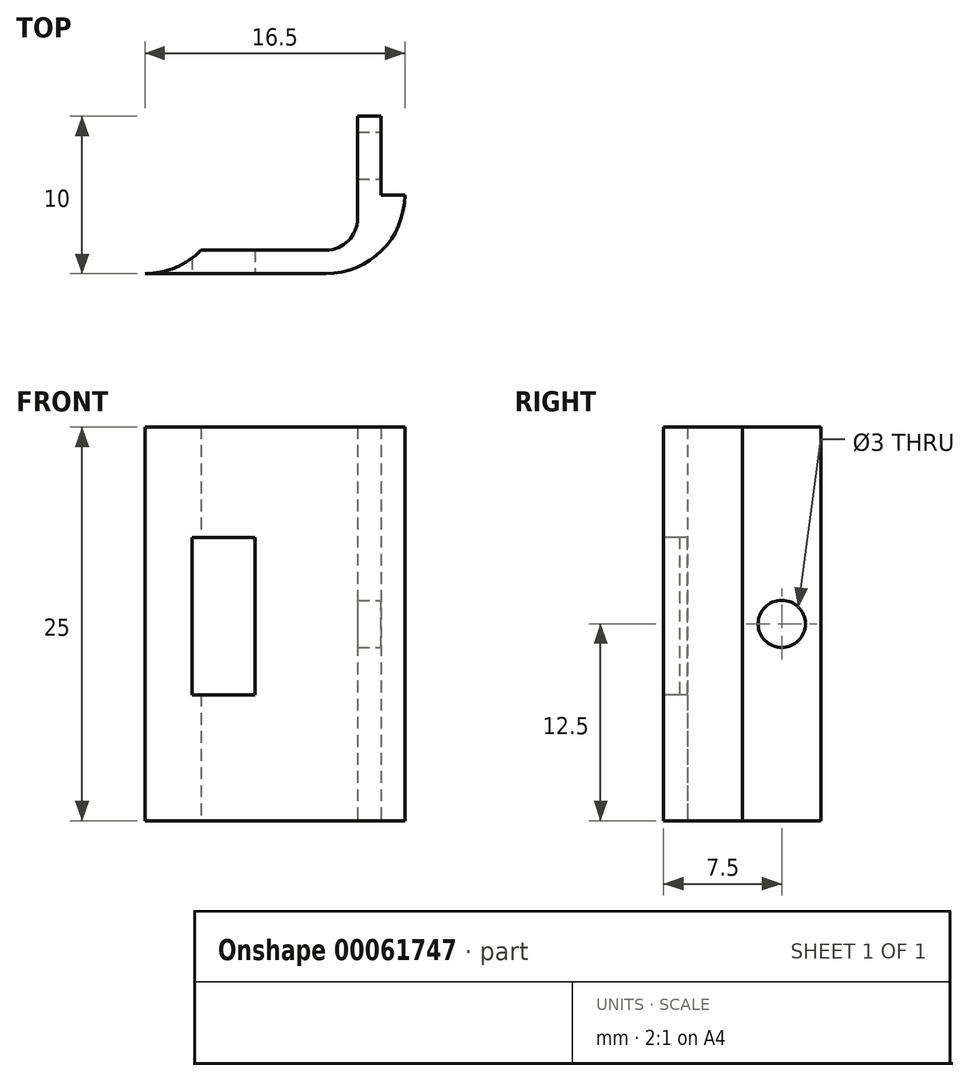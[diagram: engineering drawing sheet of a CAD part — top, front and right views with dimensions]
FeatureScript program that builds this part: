
annotation { "Feature Type Name" : "Feature", "Feature Type Description" : "" }
export const myFeature = defineFeature(function(context is Context, id is Id, definition is map)
    precondition{}
    {
        {
            var Q0;
            Q0=qCreatedBy(makeId("Top.planeOp"),FACE);
            var sketch = newSketch(context, id + "F0", { "sketchPlane" : qUnion([Q0])});
            skLineSegment(sketch, "E0", {"start": v(0, 0) * mm, "end": v(11.5, 0) * mm});
            skArc(sketch, "E1.filletArc", {"start": v(11.5, 0) * mm, "mid": v(15.04, 1.46) * mm, "end": v(16.5, 5) * mm});
            skLineSegment(sketch, "E2.1", {"start": v(0, 1.5) * mm, "end": v(10, 1.5) * mm});
            skLineSegment(sketch, "E3", {"start": v(0, 1.5) * mm, "end": v(0, 0) * mm});
            skCircle(sketch, "E4", {"center": v(0, 5) * mm, "radius": 5 * mm, "construction": true});
            skLineSegment(sketch, "E5", {"start": v(0, 1.5) * mm, "end": v(0, 8.16) * mm, "construction": true});
            skPoint(sketch, "E6", {"position": v(3.57, 1.5) * mm});
            skArc(sketch, "E7", {"start": v(0, 0) * mm, "mid": v(1.94, 0.4) * mm, "end": v(3.57, 1.5) * mm});
            skLineSegment(sketch, "E8", {"start": v(16.5, 5) * mm, "end": v(15, 5) * mm});
            skLineSegment(sketch, "E9", {"start": v(15, 5) * mm, "end": v(13.5, 5) * mm});
            skLineSegment(sketch, "E10", {"start": v(13.5, 5) * mm, "end": v(13.5, 10) * mm});
            skLineSegment(sketch, "E11", {"start": v(13.5, 10) * mm, "end": v(15, 10) * mm});
            skLineSegment(sketch, "E12", {"start": v(15, 10) * mm, "end": v(15, 5) * mm});
            skLineSegment(sketch, "E13", {"start": v(10, 1.5) * mm, "end": v(11.5, 1.5) * mm});
            skLineSegment(sketch, "E14", {"start": v(13.5, 3.5) * mm, "end": v(13.5, 5) * mm});
            skPoint(sketch, "E15.visualSharp", {"position": v(13.5, 1.5) * mm});
            skArc(sketch, "E15.filletArc", {"start": v(11.5, 1.5) * mm, "mid": v(12.91, 2.09) * mm, "end": v(13.5, 3.5) * mm});
            skSolve(sketch);
        }
        {
            var Q0;
            Q0=makeQuery(id+"F0.imprint","IMPRINT",FACE,{"disambiguationData":[TD([[makeQuery(id+"F0.imprint","IMPRINT",EDGE,{"derivedFrom":sQuery(id+"F0.wireOp",EDGE,"E0")}),1.0]])]});
            var Q1;
            Q1=makeQuery(id+"F0.imprint","IMPRINT",FACE,{"disambiguationData":[TD([[makeQuery(id+"F0.imprint","IMPRINT",EDGE,{"derivedFrom":sQuery(id+"F0.wireOp",EDGE,"E9")}),-1.0]])]});
            extrude(context, id + "F1", {"entities" : qUnion([Q0, Q1]), "depth" : 25 * mm});
        }
        {
            var Q0;
            Q0=makeQuery(id+"F1.opExtrude","SWEPT_FACE",FACE,{"disambiguationData":[OSD([sQuery(id+"F0.wireOp",EDGE,"E12")])]});
            var sketch = newSketch(context, id + "F2", { "sketchPlane" : qUnion([Q0])});
            skCircle(sketch, "E16", {"center": v(7.5, 12.5) * mm, "radius": 1.5 * mm});
            skPoint(sketch, "E17", {"position": v(7.5, 25) * mm});
            skPoint(sketch, "E18", {"position": v(-40.9, 34.48) * mm});
            skLineSegment(sketch, "E19", {"start": v(7.5, 25) * mm, "end": v(7.5, 0) * mm, "construction": true});
            skPoint(sketch, "E20", {"position": v(10, 12.5) * mm});
            skLineSegment(sketch, "E21", {"start": v(10, 12.5) * mm, "end": v(5, 12.5) * mm, "construction": true});
            skSolve(sketch);
        }
        {
            var Q0;
            Q0=makeQuery(id+"F2.imprint","IMPRINT",FACE,{"disambiguationData":[TD([[makeQuery(id+"F2.imprint","IMPRINT",EDGE,{"derivedFrom":sQuery(id+"F2.wireOp",EDGE,"E16")}),1.0]])]});
            extrude(context, id + "F3", {"entities" : qUnion([Q0]), "operationType" : NewBodyOperationType.REMOVE, "oppositeDirection" : true, "depth" : 25 * mm});
        }
        {
            var Q0;
            Q0=makeQuery(id+"F1.opExtrude","SWEPT_FACE",FACE,{"disambiguationData":[OSD([sQuery(id+"F0.wireOp",EDGE,"E0")])]});
            var sketch = newSketch(context, id + "F4", { "sketchPlane" : qUnion([Q0])});
            skLineSegment(sketch, "E22.bottom", {"start": v(3, 18) * mm, "end": v(7, 18) * mm});
            skLineSegment(sketch, "E22.top", {"start": v(3, 8) * mm, "end": v(7, 8) * mm});
            skLineSegment(sketch, "E22.left", {"start": v(3, 18) * mm, "end": v(3, 8) * mm});
            skLineSegment(sketch, "E22.right", {"start": v(7, 18) * mm, "end": v(7, 8) * mm});
            skSolve(sketch);
        }
        {
            var Q0;
            Q0=makeQuery(id+"F4.imprint","IMPRINT",FACE,{"disambiguationData":[TD([[makeQuery(id+"F4.imprint","IMPRINT",EDGE,{"derivedFrom":sQuery(id+"F4.wireOp",EDGE,"E22.bottom")}),-1.0]])]});
            extrude(context, id + "F5", {"entities" : qUnion([Q0]), "operationType" : NewBodyOperationType.REMOVE, "oppositeDirection" : true, "depth" : 25 * mm});
        }
    });
